# Revit family: Geräteeinsätze GES_Geräteeinsatz_GES2_mit_Griffbügel
name_source: partatom
category: Generic Models
revit_build: Autodesk Revit 2015 (Build: 20140606_1530(x64)
units: mm (PartAtom-declared; Revit-internal decimal feet)

## types (3) — shared parameters
Height = 61 mm  [stored 0.200131 ft]
Inner cut = 92 mm  [stored 0.301837 ft]
Inner cut2 = 136 mm  [stored 0.446194 ft]
Lenght = 194 mm  [stored 0.636483 ft]
Lenght 2 = 180 mm  [stored 0.590551 ft]
Manufacturer = OBO Bettermann
Snur width = 69 mm
URL = http://www.obo-bettermann.com
Width = 118 mm
Width 2 = 104 mm  [stored 0.341207 ft]

## per-type parameters (varying)
| type | GTIN | Manufacturer Art. No. | Material |
| GES2 U 9011 | 4012195102229
4012196331864 | 7405120 | Plastic RAL 9011 |
| GES2 U 7011 | 4012195102182
4012195102182 | 7405116 | Plastic RAL 7011 |
| GES2 U 1019 | 4012195102236 | 7405124 | Plastic RAL 1019 |

note: column(s) folded — value = type name in every type: Article Type

note: [stored X ft] marks values corroborated as IEEE doubles in the binary element streams (Revit-internal decimal feet)

## geometry (parser evidence)
native form markers: Sweep x2
no freeform markers — native parametric forms only
